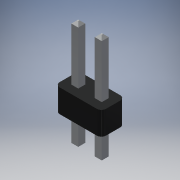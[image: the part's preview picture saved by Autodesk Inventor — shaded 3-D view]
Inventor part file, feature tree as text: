
AUTODESK INVENTOR PART (.ipt)
format: ipt  version: 2019.4 (Build 234330000, 330)  size: 125,440 bytes
history: native  units: mm
features: chamfer x1
ambient origin geometry x8: Origin, YZ Plane, XZ Plane, XY Plane, X Axis, Y Axis, Z Axis, Center Point
bodies: Solid1 (feature_tree)
feature tree (1):
  chamfer  "Chamfer1"  [1 undecoded]
note: 1 required parameter value undecoded (feature->parameter linkage not recoverable at this tier; creation-order binding heuristic only, values carry confidence <= 0.55)
